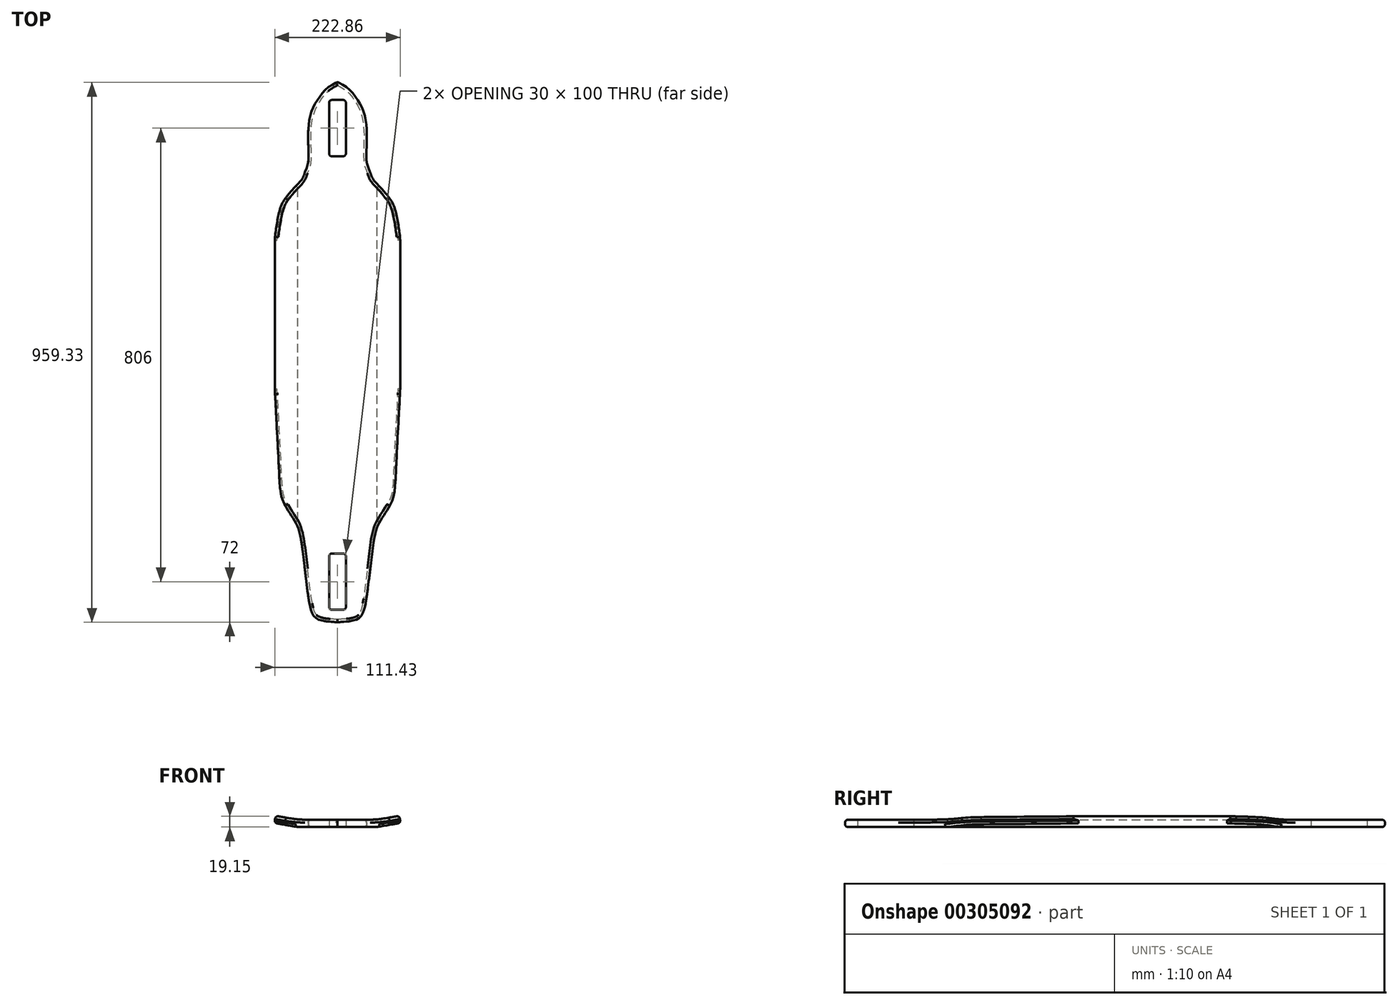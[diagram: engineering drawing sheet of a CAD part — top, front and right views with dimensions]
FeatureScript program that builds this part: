
annotation { "Feature Type Name" : "Feature", "Feature Type Description" : "" }
export const myFeature = defineFeature(function(context is Context, id is Id, definition is map)
    precondition{}
    {
        {
            var Q0;
            Q0=qCreatedBy(makeId("Front.planeOp"),FACE);
            var sketch = newSketch(context, id + "F0", { "sketchPlane" : qUnion([Q0])});
            skLineSegment(sketch, "E0.bottom", {"start": v(70.6, 6.5) * mm, "end": v(0, 6.5) * mm});
            skLineSegment(sketch, "E0.top", {"start": v(70.6, -6.5) * mm, "end": v(0, -6.5) * mm});
            skLineSegment(sketch, "E0.left", {"start": v(70.6, 6.5) * mm, "end": v(70.6, -6.5) * mm});
            skPoint(sketch, "E0.middle", {"position": v(0, 0) * mm});
            skLineSegment(sketch, "E1", {"start": v(70.6, 6.5) * mm, "end": v(110, 13.45) * mm});
            skLineSegment(sketch, "E2", {"start": v(110, 13.45) * mm, "end": v(112.22, 0.84) * mm});
            skLineSegment(sketch, "E3", {"start": v(112.22, 0.84) * mm, "end": v(70.6, -6.5) * mm});
            skLineSegment(sketch, "E4", {"start": v(0, 6.5) * mm, "end": v(0, -6.5) * mm});
            skPoint(sketch, "E0.right.end.orphan", {"position": v(-70.6, -6.5) * mm});
            skPoint(sketch, "E0.right.start.orphan", {"position": v(-70.6, 6.5) * mm});
            skLineSegment(sketch, "E5.MirrorCS", {"start": v(-70.6, 6.5) * mm, "end": v(0, 6.5) * mm});
            skLineSegment(sketch, "E6.MirrorCS", {"start": v(-70.6, -6.5) * mm, "end": v(0, -6.5) * mm});
            skLineSegment(sketch, "E7.MirrorCS", {"start": v(-110, 13.45) * mm, "end": v(-112.22, 0.84) * mm});
            skLineSegment(sketch, "E8.MirrorCS", {"start": v(-70.6, 6.5) * mm, "end": v(-110, 13.45) * mm});
            skLineSegment(sketch, "E9.MirrorCS", {"start": v(-112.22, 0.84) * mm, "end": v(-70.6, -6.5) * mm});
            skLineSegment(sketch, "E10.MirrorCS", {"start": v(-70.6, 6.5) * mm, "end": v(-70.6, -6.5) * mm});
            skSolve(sketch);
        }
        {
            var Q0;
            Q0=makeQuery(id+"F0.imprint","IMPRINT",FACE,{"disambiguationData":[TD([[makeQuery(id+"F0.imprint","IMPRINT",EDGE,{"derivedFrom":sQuery(id+"F0.wireOp",EDGE,"E0.left")}),1.0]])]});
            var Q1;
            Q1=makeQuery(id+"F0.imprint","IMPRINT",FACE,{"disambiguationData":[TD([[makeQuery(id+"F0.imprint","IMPRINT",EDGE,{"derivedFrom":sQuery(id+"F0.wireOp",EDGE,"E0.bottom")}),1.0]])]});
            var Q2;
            Q2=makeQuery(id+"F0.imprint","IMPRINT",FACE,{"disambiguationData":[TD([[makeQuery(id+"F0.imprint","IMPRINT",EDGE,{"derivedFrom":sQuery(id+"F0.wireOp",EDGE,"E4")}),-1.0]])]});
            var Q3;
            Q3=makeQuery(id+"F0.imprint","IMPRINT",FACE,{"disambiguationData":[TD([[makeQuery(id+"F0.imprint","IMPRINT",EDGE,{"derivedFrom":sQuery(id+"F0.wireOp",EDGE,"E7.MirrorCS")}),1.0]])]});
            extrude(context, id + "F1", {"entities" : qUnion([Q0, Q1, Q2, Q3]), "depth" : 500 * mm, "hasSecondDirection" : true, "secondDirectionOppositeDirection" : true, "secondDirectionDepth" : 460 * mm});
        }
        {
            var Q0;
            Q0=qCreatedBy(makeId("Top.planeOp"),FACE);
            var sketch = newSketch(context, id + "F2", { "sketchPlane" : qUnion([Q0])});
            skLineSegment(sketch, "E11.0", {"start": v(70.6, 460) * mm, "end": v(-70.6, 460) * mm});
            skPoint(sketch, "E12", {"position": v(0, 460) * mm});
            skFitSpline(sketch, "E13", {"points": [v(0, 460) * mm, v(-20.2, 447.47) * mm, v(-31.54, 434.07) * mm, v(-40.81, 419.65) * mm, v(-47.34, 403.85) * mm, v(-51.8, 377.07) * mm, v(-51.8, 345.48) * mm, v(-51.46, 322.47) * mm, v(-53.17, 312.17) * mm, v(-57.64, 300.5) * mm, v(-63.13, 287.38) * mm, v(-74.64, 274.58) * mm, v(-87.44, 259.86) * mm, v(-98.32, 244.19) * mm, v(-106, 217.63) * mm, v(-112.22, 159.13) * mm], "startDerivative": vector(-314.65, -167.43) * mm, "endDerivative": vector(0, -598.4) * mm});
            skLineSegment(sketch, "E14.0", {"start": v(-112.22, -500) * mm, "end": v(-112.22, 460) * mm});
            skLineSegment(sketch, "E15", {"start": v(0, 460) * mm, "end": v(0, 394.27) * mm});
            skFitSpline(sketch, "E16.MirrorCS", {"points": [v(0, 460) * mm, v(20.2, 447.47) * mm, v(31.54, 434.07) * mm, v(40.81, 419.65) * mm, v(47.34, 403.85) * mm, v(51.8, 377.07) * mm, v(51.8, 345.48) * mm, v(51.46, 322.47) * mm, v(53.17, 312.17) * mm, v(57.64, 300.5) * mm, v(63.13, 287.38) * mm, v(74.64, 274.58) * mm, v(87.44, 259.86) * mm, v(98.32, 244.19) * mm, v(106, 217.63) * mm, v(112.22, 159.13) * mm], "startDerivative": vector(314.65, -167.43) * mm, "endDerivative": vector(0, -598.4) * mm});
            skLineSegment(sketch, "E17.0", {"start": v(70.6, -500) * mm, "end": v(-70.6, -500) * mm});
            skFitSpline(sketch, "E18", {"points": [v(0, -500) * mm, v(-35.93, -494.36) * mm, v(-49.08, -470.55) * mm, v(-64.74, -354.03) * mm, v(-76.65, -318.95) * mm, v(-96.7, -285.12) * mm, v(-103.59, -237.5) * mm, v(-112.22, -70.7) * mm], "startDerivative": vector(-372.72, 17.38) * mm, "endDerivative": vector(-43.29, 806.97) * mm});
            skLineSegment(sketch, "E19", {"start": v(-112.22, 159.13) * mm, "end": v(-112.22, -70.7) * mm});
            skLineSegment(sketch, "E20.MirrorCS", {"start": v(112.22, 159.13) * mm, "end": v(112.22, -70.7) * mm});
            skLineSegment(sketch, "E21.0", {"start": v(112.22, -500) * mm, "end": v(112.22, 460) * mm});
            skLineSegment(sketch, "E22.0", {"start": v(112.22, -500) * mm, "end": v(70.6, -500) * mm});
            skLineSegment(sketch, "E23.0", {"start": v(-112.22, -500) * mm, "end": v(-70.6, -500) * mm});
            skLineSegment(sketch, "E24.0", {"start": v(112.22, 460) * mm, "end": v(70.6, 460) * mm});
            skLineSegment(sketch, "E25.0", {"start": v(-112.22, 460) * mm, "end": v(-70.6, 460) * mm});
            skLineSegment(sketch, "E26.bottom", {"start": v(-112.22, 460) * mm, "end": v(112.22, 460) * mm});
            skLineSegment(sketch, "E26.top", {"start": v(-112.22, -500) * mm, "end": v(112.22, -500) * mm});
            skLineSegment(sketch, "E26.left", {"start": v(-112.22, 460) * mm, "end": v(-112.22, -500) * mm});
            skLineSegment(sketch, "E26.right", {"start": v(112.22, 460) * mm, "end": v(112.22, -500) * mm});
            skFitSpline(sketch, "E27.MirrorCS", {"points": [v(0, -500) * mm, v(35.93, -494.36) * mm, v(49.08, -470.55) * mm, v(64.74, -354.03) * mm, v(76.65, -318.95) * mm, v(96.7, -285.12) * mm, v(103.59, -237.5) * mm, v(112.22, -70.7) * mm], "startDerivative": vector(372.72, 17.38) * mm, "endDerivative": vector(43.29, 806.97) * mm});
            skSolve(sketch);
        }
        {
            var Q0;
            {var subQ0=sQuery(id+"F2.wireOp",EDGE,"E27.MirrorCS");Q0=makeQuery(id+"F2.imprint","IMPRINT",FACE,{"disambiguationData":[TD([[makeQuery(id+"F2.imprint","IMPRINT",EDGE,{"derivedFrom":subQ0}),-1.0]])]});}
            var Q1;
            {var subQ0=sQuery(id+"F2.wireOp",EDGE,"E18");Q1=makeQuery(id+"F2.imprint","IMPRINT",FACE,{"disambiguationData":[TD([[makeQuery(id+"F2.imprint","IMPRINT",EDGE,{"derivedFrom":subQ0}),1.0]])]});}
            var Q2;
            {var subQ0=sQuery(id+"F2.wireOp",EDGE,"E13");Q2=makeQuery(id+"F2.imprint","IMPRINT",FACE,{"disambiguationData":[TD([[makeQuery(id+"F2.imprint","IMPRINT",EDGE,{"derivedFrom":subQ0}),-1.0]])]});}
            var Q3;
            {var subQ0=sQuery(id+"F2.wireOp",EDGE,"E16.MirrorCS");Q3=makeQuery(id+"F2.imprint","IMPRINT",FACE,{"disambiguationData":[TD([[makeQuery(id+"F2.imprint","IMPRINT",EDGE,{"derivedFrom":subQ0}),1.0]])]});}
            extrude(context, id + "F3", {"entities" : qUnion([Q0, Q1, Q2, Q3]), "operationType" : NewBodyOperationType.REMOVE, "oppositeDirection" : true, "depth" : 25 * mm, "hasSecondDirection" : true, "secondDirectionOppositeDirection" : false, "secondDirectionDepth" : 25 * mm});
        }
        {
            var Q0;
            Q0=makeQuery(id+"F1.opExtrude","SWEPT_EDGE",EDGE,{"disambiguationData":[OSD([sQuery(id+"F0.wireOp",EDGE,"E5.MirrorCS"),sQuery(id+"F0.wireOp",EDGE,"E8.MirrorCS"),sQuery(id+"F0.wireOp",EDGE,"E10.MirrorCS")])]});
            var Q1;
            Q1=makeQuery(id+"F1.opExtrude","SWEPT_EDGE",EDGE,{"disambiguationData":[OSD([sQuery(id+"F0.wireOp",EDGE,"E0.bottom"),sQuery(id+"F0.wireOp",EDGE,"E0.left"),sQuery(id+"F0.wireOp",EDGE,"E1")])]});
            fillet(context, id + "F4", {"entities" : qUnion([Q0, Q1]), "radius" : 200 * mm, "tangentPropagation" : true, "allowEdgeOverflow" : false});
        }
        {
            var Q0;
            Q0=makeQuery(id+"F1.opExtrude","SWEPT_FACE",FACE,{"disambiguationData":[OSD([sQuery(id+"F0.wireOp",EDGE,"E0.top"),sQuery(id+"F0.wireOp",EDGE,"E6.MirrorCS")])]});
            var sketch = newSketch(context, id + "F5", { "sketchPlane" : qUnion([Q0])});
            skLineSegment(sketch, "E28.bottom", {"start": v(15, -428) * mm, "end": v(-15, -428) * mm});
            skLineSegment(sketch, "E28.top", {"start": v(15, -328) * mm, "end": v(-15, -328) * mm});
            skLineSegment(sketch, "E28.left", {"start": v(15, -428) * mm, "end": v(15, -328) * mm});
            skLineSegment(sketch, "E28.right", {"start": v(-15, -428) * mm, "end": v(-15, -328) * mm});
            skPoint(sketch, "E28.middle", {"position": v(0, -378) * mm});
            skLineSegment(sketch, "E29.bottom", {"start": v(15, 378) * mm, "end": v(-15, 378) * mm});
            skLineSegment(sketch, "E29.top", {"start": v(15, 478) * mm, "end": v(-15, 478) * mm});
            skLineSegment(sketch, "E29.left", {"start": v(15, 378) * mm, "end": v(15, 478) * mm});
            skLineSegment(sketch, "E29.right", {"start": v(-15, 378) * mm, "end": v(-15, 478) * mm});
            skPoint(sketch, "E29.middle", {"position": v(0, 428) * mm});
            skLineSegment(sketch, "E30.0", {"start": v(-112.22, 500) * mm, "end": v(112.22, 500) * mm});
            skSolve(sketch);
        }
        {
            var Q0;
            Q0 = qSketchRegion(id + "F5", true);
            extrude(context, id + "F6", {"entities" : qUnion([Q0]), "operationType" : NewBodyOperationType.REMOVE, "oppositeDirection" : true, "depth" : 25 * mm, "hasSecondDirection" : true, "secondDirectionOppositeDirection" : false, "secondDirectionDepth" : 25 * mm});
        }
        {
            var Q0;
            Q0=makeQuery(id+"F1.opExtrude","SWEPT_EDGE",EDGE,{"disambiguationData":[OSD([sQuery(id+"F0.wireOp",EDGE,"E7.MirrorCS"),sQuery(id+"F0.wireOp",EDGE,"E8.MirrorCS")])]});
            var Q1;
            Q1=makeQuery(id+"F3.boolean.opBoolean","INTERSECT",EDGE,{"derivedFrom":[makeQuery(id+"F1.opExtrude","SWEPT_FACE",FACE,{"disambiguationData":[OSD([sQuery(id+"F0.wireOp",EDGE,"E8.MirrorCS")])]}),makeQuery(id+"F3.opExtrude","SWEPT_FACE",FACE,{"disambiguationData":[OSD([sQuery(id+"F2.wireOp",EDGE,"E13")])]})]});
            var Q2;
            Q2=makeQuery(id+"F3.boolean.opBoolean","INTERSECT",EDGE,{"derivedFrom":[makeQuery(id+"F1.opExtrude","SWEPT_FACE",FACE,{"disambiguationData":[OSD([sQuery(id+"F0.wireOp",EDGE,"E0.bottom"),sQuery(id+"F0.wireOp",EDGE,"E5.MirrorCS")])]}),makeQuery(id+"F3.opExtrude","SWEPT_FACE",FACE,{"disambiguationData":[OSD([sQuery(id+"F2.wireOp",EDGE,"E13")])]})]});
            var Q3;
            Q3=makeQuery(id+"F3.boolean.opBoolean","INTERSECT",EDGE,{"derivedFrom":[makeQuery(id+"F1.opExtrude","SWEPT_FACE",FACE,{"disambiguationData":[OSD([sQuery(id+"F0.wireOp",EDGE,"E0.bottom"),sQuery(id+"F0.wireOp",EDGE,"E5.MirrorCS")])]}),makeQuery(id+"F3.opExtrude","SWEPT_FACE",FACE,{"disambiguationData":[OSD([sQuery(id+"F2.wireOp",EDGE,"E16.MirrorCS")])]})]});
            var Q4;
            Q4=makeQuery(id+"F3.boolean.opBoolean","INTERSECT",EDGE,{"derivedFrom":[makeQuery(id+"F1.opExtrude","SWEPT_FACE",FACE,{"disambiguationData":[OSD([sQuery(id+"F0.wireOp",EDGE,"E1")])]}),makeQuery(id+"F3.opExtrude","SWEPT_FACE",FACE,{"disambiguationData":[OSD([sQuery(id+"F2.wireOp",EDGE,"E16.MirrorCS")])]})]});
            var Q5;
            Q5=makeQuery(id+"F1.opExtrude","SWEPT_EDGE",EDGE,{"disambiguationData":[OSD([sQuery(id+"F0.wireOp",EDGE,"E1"),sQuery(id+"F0.wireOp",EDGE,"E2")])]});
            var Q6;
            Q6=makeQuery(id+"F3.boolean.opBoolean","INTERSECT",EDGE,{"derivedFrom":[makeQuery(id+"F1.opExtrude","SWEPT_FACE",FACE,{"disambiguationData":[OSD([sQuery(id+"F0.wireOp",EDGE,"E1")])]}),makeQuery(id+"F3.opExtrude","SWEPT_FACE",FACE,{"disambiguationData":[OSD([sQuery(id+"F2.wireOp",EDGE,"E27.MirrorCS")])]})]});
            var Q7;
            Q7=makeQuery(id+"F3.boolean.opBoolean","INTERSECT",EDGE,{"derivedFrom":[makeQuery(id+"F1.opExtrude","SWEPT_FACE",FACE,{"disambiguationData":[OSD([sQuery(id+"F0.wireOp",EDGE,"E0.bottom"),sQuery(id+"F0.wireOp",EDGE,"E5.MirrorCS")])]}),makeQuery(id+"F3.opExtrude","SWEPT_FACE",FACE,{"disambiguationData":[OSD([sQuery(id+"F2.wireOp",EDGE,"E27.MirrorCS")])]})]});
            var Q8;
            Q8=makeQuery(id+"F3.boolean.opBoolean","INTERSECT",EDGE,{"derivedFrom":[makeQuery(id+"F1.opExtrude","SWEPT_FACE",FACE,{"disambiguationData":[OSD([sQuery(id+"F0.wireOp",EDGE,"E0.bottom"),sQuery(id+"F0.wireOp",EDGE,"E5.MirrorCS")])]}),makeQuery(id+"F3.opExtrude","SWEPT_FACE",FACE,{"disambiguationData":[OSD([sQuery(id+"F2.wireOp",EDGE,"E18")])]})]});
            var Q9;
            Q9=makeQuery(id+"F3.boolean.opBoolean","INTERSECT",EDGE,{"derivedFrom":[makeQuery(id+"F1.opExtrude","SWEPT_FACE",FACE,{"disambiguationData":[OSD([sQuery(id+"F0.wireOp",EDGE,"E8.MirrorCS")])]}),makeQuery(id+"F3.opExtrude","SWEPT_FACE",FACE,{"disambiguationData":[OSD([sQuery(id+"F2.wireOp",EDGE,"E18")])]})]});
            var Q10;
            Q10=makeQuery(id+"F3.boolean.opBoolean","INTERSECT",EDGE,{"derivedFrom":[makeQuery(id+"F1.opExtrude","SWEPT_FACE",FACE,{"disambiguationData":[OSD([sQuery(id+"F0.wireOp",EDGE,"E9.MirrorCS")])]}),makeQuery(id+"F3.opExtrude","SWEPT_FACE",FACE,{"disambiguationData":[OSD([sQuery(id+"F2.wireOp",EDGE,"E18")])]})]});
            var Q11;
            Q11=makeQuery(id+"F1.opExtrude","SWEPT_EDGE",EDGE,{"disambiguationData":[OSD([sQuery(id+"F0.wireOp",EDGE,"E7.MirrorCS"),sQuery(id+"F0.wireOp",EDGE,"E9.MirrorCS")])]});
            var Q12;
            Q12=makeQuery(id+"F3.boolean.opBoolean","INTERSECT",EDGE,{"derivedFrom":[makeQuery(id+"F1.opExtrude","SWEPT_FACE",FACE,{"disambiguationData":[OSD([sQuery(id+"F0.wireOp",EDGE,"E9.MirrorCS")])]}),makeQuery(id+"F3.opExtrude","SWEPT_FACE",FACE,{"disambiguationData":[OSD([sQuery(id+"F2.wireOp",EDGE,"E13")])]})]});
            var Q13;
            Q13=makeQuery(id+"F3.boolean.opBoolean","INTERSECT",EDGE,{"derivedFrom":[makeQuery(id+"F1.opExtrude","SWEPT_FACE",FACE,{"disambiguationData":[OSD([sQuery(id+"F0.wireOp",EDGE,"E0.top"),sQuery(id+"F0.wireOp",EDGE,"E6.MirrorCS")])]}),makeQuery(id+"F3.opExtrude","SWEPT_FACE",FACE,{"disambiguationData":[OSD([sQuery(id+"F2.wireOp",EDGE,"E13")])]})]});
            var Q14;
            Q14=makeQuery(id+"F3.boolean.opBoolean","INTERSECT",EDGE,{"derivedFrom":[makeQuery(id+"F1.opExtrude","SWEPT_FACE",FACE,{"disambiguationData":[OSD([sQuery(id+"F0.wireOp",EDGE,"E0.top"),sQuery(id+"F0.wireOp",EDGE,"E6.MirrorCS")])]}),makeQuery(id+"F3.opExtrude","SWEPT_FACE",FACE,{"disambiguationData":[OSD([sQuery(id+"F2.wireOp",EDGE,"E16.MirrorCS")])]})]});
            var Q15;
            Q15=makeQuery(id+"F3.boolean.opBoolean","INTERSECT",EDGE,{"derivedFrom":[makeQuery(id+"F1.opExtrude","SWEPT_FACE",FACE,{"disambiguationData":[OSD([sQuery(id+"F0.wireOp",EDGE,"E3")])]}),makeQuery(id+"F3.opExtrude","SWEPT_FACE",FACE,{"disambiguationData":[OSD([sQuery(id+"F2.wireOp",EDGE,"E16.MirrorCS")])]})]});
            var Q16;
            Q16=makeQuery(id+"F3.boolean.opBoolean","INTERSECT",EDGE,{"derivedFrom":[makeQuery(id+"F1.opExtrude","SWEPT_FACE",FACE,{"disambiguationData":[OSD([sQuery(id+"F0.wireOp",EDGE,"E3")])]}),makeQuery(id+"F3.opExtrude","SWEPT_FACE",FACE,{"disambiguationData":[OSD([sQuery(id+"F2.wireOp",EDGE,"E27.MirrorCS")])]})]});
            var Q17;
            Q17=makeQuery(id+"F3.boolean.opBoolean","INTERSECT",EDGE,{"derivedFrom":[makeQuery(id+"F1.opExtrude","SWEPT_FACE",FACE,{"disambiguationData":[OSD([sQuery(id+"F0.wireOp",EDGE,"E0.top"),sQuery(id+"F0.wireOp",EDGE,"E6.MirrorCS")])]}),makeQuery(id+"F3.opExtrude","SWEPT_FACE",FACE,{"disambiguationData":[OSD([sQuery(id+"F2.wireOp",EDGE,"E27.MirrorCS")])]})]});
            var Q18;
            Q18=makeQuery(id+"F3.boolean.opBoolean","INTERSECT",EDGE,{"derivedFrom":[makeQuery(id+"F1.opExtrude","SWEPT_FACE",FACE,{"disambiguationData":[OSD([sQuery(id+"F0.wireOp",EDGE,"E0.top"),sQuery(id+"F0.wireOp",EDGE,"E6.MirrorCS")])]}),makeQuery(id+"F3.opExtrude","SWEPT_FACE",FACE,{"disambiguationData":[OSD([sQuery(id+"F2.wireOp",EDGE,"E18")])]})]});
            fillet(context, id + "F7", {"entities" : qUnion([Q0, Q1, Q2, Q3, Q4, Q5, Q6, Q7, Q8, Q9, Q10, Q11, Q12, Q13, Q14, Q15, Q16, Q17, Q18]), "radius" : 5 * mm, "tangentPropagation" : true, "allowEdgeOverflow" : false});
        }
        {
            var Q0;
            {var subQ0=makeQuery(id+"F1.opExtrude","SWEPT_FACE",FACE,{"disambiguationData":[OSD([sQuery(id+"F0.wireOp",EDGE,"E0.bottom"),sQuery(id+"F0.wireOp",EDGE,"E5.MirrorCS")])]});Q0=makeQuery(id+"F7.opFillet","BLEND_EDGE",EDGE,{"blendedFrom":[makeQuery(id+"F3.boolean.opBoolean","INTERSECT",EDGE,{"derivedFrom":[subQ0,makeQuery(id+"F3.opExtrude","SWEPT_FACE",FACE,{"disambiguationData":[OSD([sQuery(id+"F2.wireOp",EDGE,"E13")])]})]}),makeQuery(id+"F3.boolean.opBoolean","INTERSECT",EDGE,{"derivedFrom":[subQ0,makeQuery(id+"F3.opExtrude","SWEPT_FACE",FACE,{"disambiguationData":[OSD([sQuery(id+"F2.wireOp",EDGE,"E16.MirrorCS")])]})]})],"blendedInto":[]});}
            var Q1;
            {var subQ0=sQuery(id+"F2.wireOp",EDGE,"E27.MirrorCS");var subQ1=sQuery(id+"F2.wireOp",EDGE,"E26.top");var subQ2=sQuery(id+"F2.wireOp",EDGE,"E18");Q1=makeQuery(id+"F3.boolean.opBoolean","TWEAK_EDGE",EDGE,{"derivedFrom":[makeQuery(id+"F3.opExtrude","SWEPT_EDGE",EDGE,{"disambiguationData":[OSD([subQ2,subQ1,subQ0]),ownerDisambiguation([makeQuery(id+"F3.opExtrude","SWEPT_BODY",BODY,{"disambiguationData":[OSD([subQ2,subQ1,sQuery(id+"F2.wireOp",EDGE,"E26.left")])]})])]}),makeQuery(id+"F3.opExtrude","SWEPT_EDGE",EDGE,{"disambiguationData":[OSD([subQ2,subQ1,subQ0]),ownerDisambiguation([makeQuery(id+"F3.opExtrude","SWEPT_BODY",BODY,{"disambiguationData":[OSD([subQ1,sQuery(id+"F2.wireOp",EDGE,"E26.right"),subQ0])]})])]})]});}
            var Q2;
            Q2=makeQuery(id+"F6.boolean.opBoolean","COPY",EDGE,{"derivedFrom":makeQuery(id+"F6.opExtrude","SWEPT_EDGE",EDGE,{"disambiguationData":[OSD([sQuery(id+"F5.wireOp",EDGE,"E28.top"),sQuery(id+"F5.wireOp",EDGE,"E28.right")])]})});
            var Q3;
            Q3=makeQuery(id+"F6.boolean.opBoolean","COPY",EDGE,{"derivedFrom":makeQuery(id+"F6.opExtrude","SWEPT_EDGE",EDGE,{"disambiguationData":[OSD([sQuery(id+"F5.wireOp",EDGE,"E28.top"),sQuery(id+"F5.wireOp",EDGE,"E28.left")])]})});
            var Q4;
            Q4=makeQuery(id+"F6.boolean.opBoolean","COPY",EDGE,{"derivedFrom":makeQuery(id+"F6.opExtrude","SWEPT_EDGE",EDGE,{"disambiguationData":[OSD([sQuery(id+"F5.wireOp",EDGE,"E28.bottom"),sQuery(id+"F5.wireOp",EDGE,"E28.left")])]})});
            var Q5;
            Q5=makeQuery(id+"F6.boolean.opBoolean","COPY",EDGE,{"derivedFrom":makeQuery(id+"F6.opExtrude","SWEPT_EDGE",EDGE,{"disambiguationData":[OSD([sQuery(id+"F5.wireOp",EDGE,"E28.bottom"),sQuery(id+"F5.wireOp",EDGE,"E28.right")])]})});
            var Q6;
            Q6=makeQuery(id+"F6.boolean.opBoolean","COPY",EDGE,{"derivedFrom":makeQuery(id+"F6.opExtrude","SWEPT_EDGE",EDGE,{"disambiguationData":[OSD([sQuery(id+"F5.wireOp",EDGE,"E29.bottom"),sQuery(id+"F5.wireOp",EDGE,"E29.right")])]})});
            var Q7;
            Q7=makeQuery(id+"F6.boolean.opBoolean","COPY",EDGE,{"derivedFrom":makeQuery(id+"F6.opExtrude","SWEPT_EDGE",EDGE,{"disambiguationData":[OSD([sQuery(id+"F5.wireOp",EDGE,"E29.bottom"),sQuery(id+"F5.wireOp",EDGE,"E29.left")])]})});
            var Q8;
            Q8=makeQuery(id+"F6.boolean.opBoolean","COPY",EDGE,{"derivedFrom":makeQuery(id+"F6.opExtrude","SWEPT_EDGE",EDGE,{"disambiguationData":[OSD([sQuery(id+"F5.wireOp",EDGE,"E29.top"),sQuery(id+"F5.wireOp",EDGE,"E29.left")])]})});
            var Q9;
            Q9=makeQuery(id+"F6.boolean.opBoolean","COPY",EDGE,{"derivedFrom":makeQuery(id+"F6.opExtrude","SWEPT_EDGE",EDGE,{"disambiguationData":[OSD([sQuery(id+"F5.wireOp",EDGE,"E29.top"),sQuery(id+"F5.wireOp",EDGE,"E29.right")])]})});
            fillet(context, id + "F8", {"entities" : qUnion([Q0, Q1, Q2, Q3, Q4, Q5, Q6, Q7, Q8, Q9]), "radius" : 5 * mm, "tangentPropagation" : true, "allowEdgeOverflow" : false});
        }
    });
